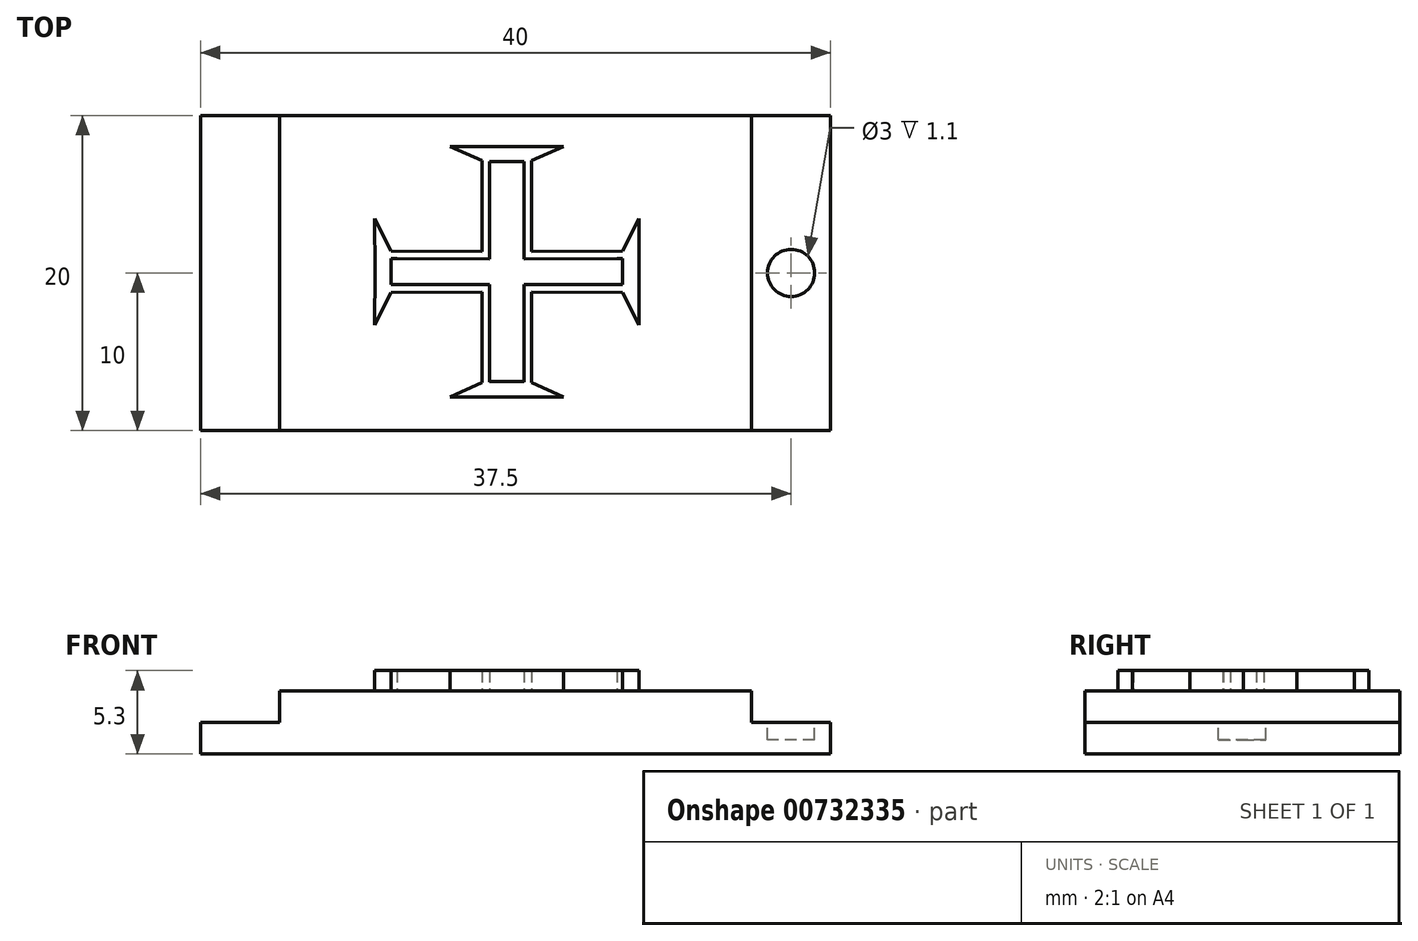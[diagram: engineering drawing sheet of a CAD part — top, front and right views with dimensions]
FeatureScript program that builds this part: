
annotation { "Feature Type Name" : "Feature", "Feature Type Description" : "" }
export const myFeature = defineFeature(function(context is Context, id is Id, definition is map)
    precondition{}
    {
        {
            var Q0;
            Q0=qCreatedBy(makeId("Top.planeOp"),FACE);
            var sketch = newSketch(context, id + "F0", { "sketchPlane" : qUnion([Q0])});
            skLineSegment(sketch, "E0.bottom", {"start": v(-30, 20) * mm, "end": v(0, 20) * mm});
            skLineSegment(sketch, "E0.top", {"start": v(-30, 0) * mm, "end": v(0, 0) * mm});
            skLineSegment(sketch, "E0.left", {"start": v(-30, 20) * mm, "end": v(-30, 0) * mm});
            skLineSegment(sketch, "E0.right", {"start": v(0, 20) * mm, "end": v(0, 0) * mm});
            skSolve(sketch);
        }
        {
            var Q0;
            Q0 = qSketchRegion(id + "F0", true);
            extrude(context, id + "F1", {"entities" : qUnion([Q0]), "depth" : 4 * mm, "offsetDistance" : 25 * mm});
        }
        {
            var Q0;
            Q0=makeQuery(id+"F1.opExtrude","CAP_FACE",FACE,{"disambiguationData":[OSD([sQuery(id+"F0.wireOp",EDGE,"E0.bottom"),sQuery(id+"F0.wireOp",EDGE,"E0.top"),sQuery(id+"F0.wireOp",EDGE,"E0.left"),sQuery(id+"F0.wireOp",EDGE,"E0.right")])],"isStart":true});
            var sketch = newSketch(context, id + "F2", { "sketchPlane" : qUnion([Q0])});
            skLineSegment(sketch, "E1.bottom", {"start": v(-30, -20) * mm, "end": v(-35, -20) * mm});
            skLineSegment(sketch, "E1.top", {"start": v(-30, 0) * mm, "end": v(-35, 0) * mm});
            skLineSegment(sketch, "E1.left", {"start": v(-30, -20) * mm, "end": v(-30, 0) * mm});
            skLineSegment(sketch, "E1.right", {"start": v(-35, -20) * mm, "end": v(-35, 0) * mm});
            skSolve(sketch);
        }
        {
            var Q0;
            Q0 = qSketchRegion(id + "F2", true);
            extrude(context, id + "F3", {"entities" : qUnion([Q0]), "operationType" : NewBodyOperationType.ADD, "oppositeDirection" : true, "depth" : 2 * mm, "offsetDistance" : 25 * mm});
        }
        {
            var Q0;
            Q0=makeQuery(id+"FZcHOp14FUNLQa1_1.boolean.opBoolean","MERGE",FACE,{"derivedFrom":[makeQuery(id+"F1.opExtrude","CAP_FACE",FACE,{"disambiguationData":[OSD([sQuery(id+"F0.wireOp",EDGE,"E0.bottom"),sQuery(id+"F0.wireOp",EDGE,"E0.top"),sQuery(id+"F0.wireOp",EDGE,"E0.left"),sQuery(id+"F0.wireOp",EDGE,"E0.right")])],"isStart":false}),makeQuery(id+"FZcHOp14FUNLQa1_1.opExtrude","CAP_FACE",FACE,{"disambiguationData":[OSD([sQuery(id+"FohpQXZtYSiY43x_1.wireOp",EDGE,"dT4UZe2O-1dsD-PJOH-Givd-Kmm09ko3N1hd.bottom"),sQuery(id+"FohpQXZtYSiY43x_1.wireOp",EDGE,"dT4UZe2O-1dsD-PJOH-Givd-Kmm09ko3N1hd.top"),sQuery(id+"FohpQXZtYSiY43x_1.wireOp",EDGE,"dT4UZe2O-1dsD-PJOH-Givd-Kmm09ko3N1hd.left"),sQuery(id+"FohpQXZtYSiY43x_1.wireOp",EDGE,"dT4UZe2O-1dsD-PJOH-Givd-Kmm09ko3N1hd.right")])],"isStart":true})]});
            var sketch = newSketch(context, id + "F4", { "sketchPlane" : qUnion([Q0])});
            skLineSegment(sketch, "E2", {"start": v(-13.97, 10.9) * mm, "end": v(-13.98, 17.13) * mm});
            skLineSegment(sketch, "E3", {"start": v(-13.98, 17.13) * mm, "end": v(-11.95, 18.04) * mm});
            skLineSegment(sketch, "E4", {"start": v(-11.95, 18.04) * mm, "end": v(-15.55, 18.04) * mm});
            skLineSegment(sketch, "E5", {"start": v(-14.46, 10.9) * mm, "end": v(-14.45, 17.07) * mm});
            skLineSegment(sketch, "E6", {"start": v(-14.45, 17.07) * mm, "end": v(-14.45, 17.07) * mm});
            skLineSegment(sketch, "E7", {"start": v(-14.45, 17.07) * mm, "end": v(-15.55, 17.07) * mm});
            skLineSegment(sketch, "E8", {"start": v(-14.46, 10.9) * mm, "end": v(-8.57, 10.9) * mm});
            skLineSegment(sketch, "E9", {"start": v(-14.46, 11.37) * mm, "end": v(-8.2, 11.4) * mm});
            skLineSegment(sketch, "E10", {"start": v(-8.2, 11.4) * mm, "end": v(-7.15, 13.47) * mm});
            skLineSegment(sketch, "E11", {"start": v(-8.57, 10.9) * mm, "end": v(-8.2, 10.9) * mm});
            skLineSegment(sketch, "E12", {"start": v(-8.2, 10.9) * mm, "end": v(-8.2, 10.08) * mm});
            skLineSegment(sketch, "E13", {"start": v(-7.15, 13.47) * mm, "end": v(-7.17, 10.08) * mm});
            skLineSegment(sketch, "E14.MirrorCS", {"start": v(-17.13, 10.9) * mm, "end": v(-17.12, 17.13) * mm});
            skLineSegment(sketch, "E15.MirrorCS", {"start": v(-17.12, 17.13) * mm, "end": v(-19.15, 18.04) * mm});
            skLineSegment(sketch, "E16.MirrorCS", {"start": v(-19.15, 18.04) * mm, "end": v(-15.55, 18.04) * mm});
            skLineSegment(sketch, "E17.MirrorCS", {"start": v(-16.65, 17.07) * mm, "end": v(-15.55, 17.07) * mm});
            skLineSegment(sketch, "E18.MirrorCS", {"start": v(-16.65, 17.07) * mm, "end": v(-16.65, 17.07) * mm});
            skLineSegment(sketch, "E19.MirrorCS", {"start": v(-16.64, 10.9) * mm, "end": v(-16.65, 17.07) * mm});
            skLineSegment(sketch, "E20.MirrorCS", {"start": v(-17.13, 9.26) * mm, "end": v(-17.12, 3.03) * mm});
            skLineSegment(sketch, "E21.MirrorCS", {"start": v(-16.64, 9.27) * mm, "end": v(-16.65, 3.1) * mm});
            skLineSegment(sketch, "E22.MirrorCS", {"start": v(-17.12, 3.03) * mm, "end": v(-19.15, 2.12) * mm});
            skLineSegment(sketch, "E23.MirrorCS", {"start": v(-16.65, 3.1) * mm, "end": v(-16.65, 3.1) * mm});
            skLineSegment(sketch, "E24.MirrorCS", {"start": v(-16.65, 3.1) * mm, "end": v(-15.55, 3.1) * mm});
            skLineSegment(sketch, "E25.MirrorCS", {"start": v(-19.15, 2.12) * mm, "end": v(-15.55, 2.12) * mm});
            skLineSegment(sketch, "E26.MirrorCS", {"start": v(-11.95, 2.12) * mm, "end": v(-15.55, 2.12) * mm});
            skLineSegment(sketch, "E27.MirrorCS", {"start": v(-14.45, 3.1) * mm, "end": v(-15.55, 3.1) * mm});
            skLineSegment(sketch, "E28.MirrorCS", {"start": v(-14.45, 3.1) * mm, "end": v(-14.45, 3.1) * mm});
            skLineSegment(sketch, "E29.MirrorCS", {"start": v(-13.98, 3.03) * mm, "end": v(-11.95, 2.12) * mm});
            skLineSegment(sketch, "E30.MirrorCS", {"start": v(-14.46, 9.27) * mm, "end": v(-14.45, 3.1) * mm});
            skLineSegment(sketch, "E31.MirrorCS", {"start": v(-13.97, 9.26) * mm, "end": v(-13.98, 3.03) * mm});
            skLineSegment(sketch, "E32.MirrorCS", {"start": v(-16.64, 11.37) * mm, "end": v(-22.9, 11.4) * mm});
            skLineSegment(sketch, "E33.MirrorCS", {"start": v(-16.64, 10.9) * mm, "end": v(-22.53, 10.9) * mm});
            skLineSegment(sketch, "E34.MirrorCS", {"start": v(-22.9, 11.4) * mm, "end": v(-23.95, 13.47) * mm});
            skLineSegment(sketch, "E35.MirrorCS", {"start": v(-22.53, 10.9) * mm, "end": v(-22.9, 10.9) * mm});
            skLineSegment(sketch, "E36.MirrorCS", {"start": v(-23.95, 13.47) * mm, "end": v(-23.93, 10.08) * mm});
            skLineSegment(sketch, "E37.MirrorCS", {"start": v(-22.9, 10.9) * mm, "end": v(-22.9, 10.08) * mm});
            skLineSegment(sketch, "E38.MirrorCS", {"start": v(-23.95, 6.7) * mm, "end": v(-23.93, 10.08) * mm});
            skLineSegment(sketch, "E39.MirrorCS", {"start": v(-22.9, 9.26) * mm, "end": v(-22.9, 10.08) * mm});
            skLineSegment(sketch, "E40.MirrorCS", {"start": v(-22.9, 8.77) * mm, "end": v(-23.95, 6.7) * mm});
            skLineSegment(sketch, "E41.MirrorCS", {"start": v(-22.53, 9.26) * mm, "end": v(-22.9, 9.26) * mm});
            skLineSegment(sketch, "E42.MirrorCS", {"start": v(-16.64, 9.27) * mm, "end": v(-22.53, 9.26) * mm});
            skLineSegment(sketch, "E43.MirrorCS", {"start": v(-16.64, 8.8) * mm, "end": v(-22.9, 8.77) * mm});
            skLineSegment(sketch, "E44.MirrorCS", {"start": v(-14.46, 9.27) * mm, "end": v(-8.57, 9.26) * mm});
            skLineSegment(sketch, "E45.MirrorCS", {"start": v(-14.46, 8.8) * mm, "end": v(-8.2, 8.77) * mm});
            skLineSegment(sketch, "E46.MirrorCS", {"start": v(-8.2, 8.77) * mm, "end": v(-7.15, 6.7) * mm});
            skLineSegment(sketch, "E47.MirrorCS", {"start": v(-8.57, 9.26) * mm, "end": v(-8.2, 9.26) * mm});
            skLineSegment(sketch, "E48.MirrorCS", {"start": v(-8.2, 9.26) * mm, "end": v(-8.2, 10.08) * mm});
            skLineSegment(sketch, "E49.MirrorCS", {"start": v(-7.15, 6.7) * mm, "end": v(-7.17, 10.08) * mm});
            skSolve(sketch);
        }
        {
            var Q0;
            Q0 = qSketchRegion(id + "F4", true);
            extrude(context, id + "F5", {"entities" : qUnion([Q0]), "operationType" : NewBodyOperationType.ADD, "depth" : 1.3 * mm, "offsetDistance" : 25 * mm});
        }
        {
            var Q0;
            Q0=makeQuery(id+"F3.boolean.opBoolean","MERGE",FACE,{"derivedFrom":[makeQuery(id+"F1.opExtrude","CAP_FACE",FACE,{"disambiguationData":[OSD([sQuery(id+"F0.wireOp",EDGE,"E0.bottom"),sQuery(id+"F0.wireOp",EDGE,"E0.top"),sQuery(id+"F0.wireOp",EDGE,"E0.left"),sQuery(id+"F0.wireOp",EDGE,"E0.right")])],"isStart":true}),makeQuery(id+"F3.opExtrude","CAP_FACE",FACE,{"disambiguationData":[OSD([sQuery(id+"F2.wireOp",EDGE,"E1.bottom"),sQuery(id+"F2.wireOp",EDGE,"E1.top"),sQuery(id+"F2.wireOp",EDGE,"E1.left"),sQuery(id+"F2.wireOp",EDGE,"E1.right")])],"isStart":true})]});
            var sketch = newSketch(context, id + "F6", { "sketchPlane" : qUnion([Q0])});
            skLineSegment(sketch, "E50.bottom", {"start": v(0, -20) * mm, "end": v(5, -20) * mm});
            skLineSegment(sketch, "E50.top", {"start": v(0, 0) * mm, "end": v(5, 0) * mm});
            skLineSegment(sketch, "E50.left", {"start": v(0, -20) * mm, "end": v(0, 0) * mm});
            skLineSegment(sketch, "E50.right", {"start": v(5, -20) * mm, "end": v(5, 0) * mm});
            skSolve(sketch);
        }
        {
            var Q0;
            Q0 = qSketchRegion(id + "F6", true);
            extrude(context, id + "F7", {"entities" : qUnion([Q0]), "operationType" : NewBodyOperationType.ADD, "oppositeDirection" : true, "depth" : 2 * mm, "offsetDistance" : 25 * mm});
        }
        {
            var Q0;
            Q0=makeQuery(id+"F7.opExtrude","CAP_FACE",FACE,{"disambiguationData":[OSD([sQuery(id+"F6.wireOp",EDGE,"E50.bottom"),sQuery(id+"F6.wireOp",EDGE,"E50.top"),sQuery(id+"F6.wireOp",EDGE,"E50.left"),sQuery(id+"F6.wireOp",EDGE,"E50.right")])],"isStart":false});
            var sketch = newSketch(context, id + "F8", { "sketchPlane" : qUnion([Q0])});
            skCircle(sketch, "E51", {"center": v(2.5, 10) * mm, "radius": 1.5 * mm});
            skSolve(sketch);
        }
        {
            var Q0;
            Q0 = qSketchRegion(id + "F8", true);
            extrude(context, id + "F9", {"entities" : qUnion([Q0]), "operationType" : NewBodyOperationType.REMOVE, "oppositeDirection" : true, "depth" : 1.1 * mm, "offsetDistance" : 25 * mm});
        }
    });
